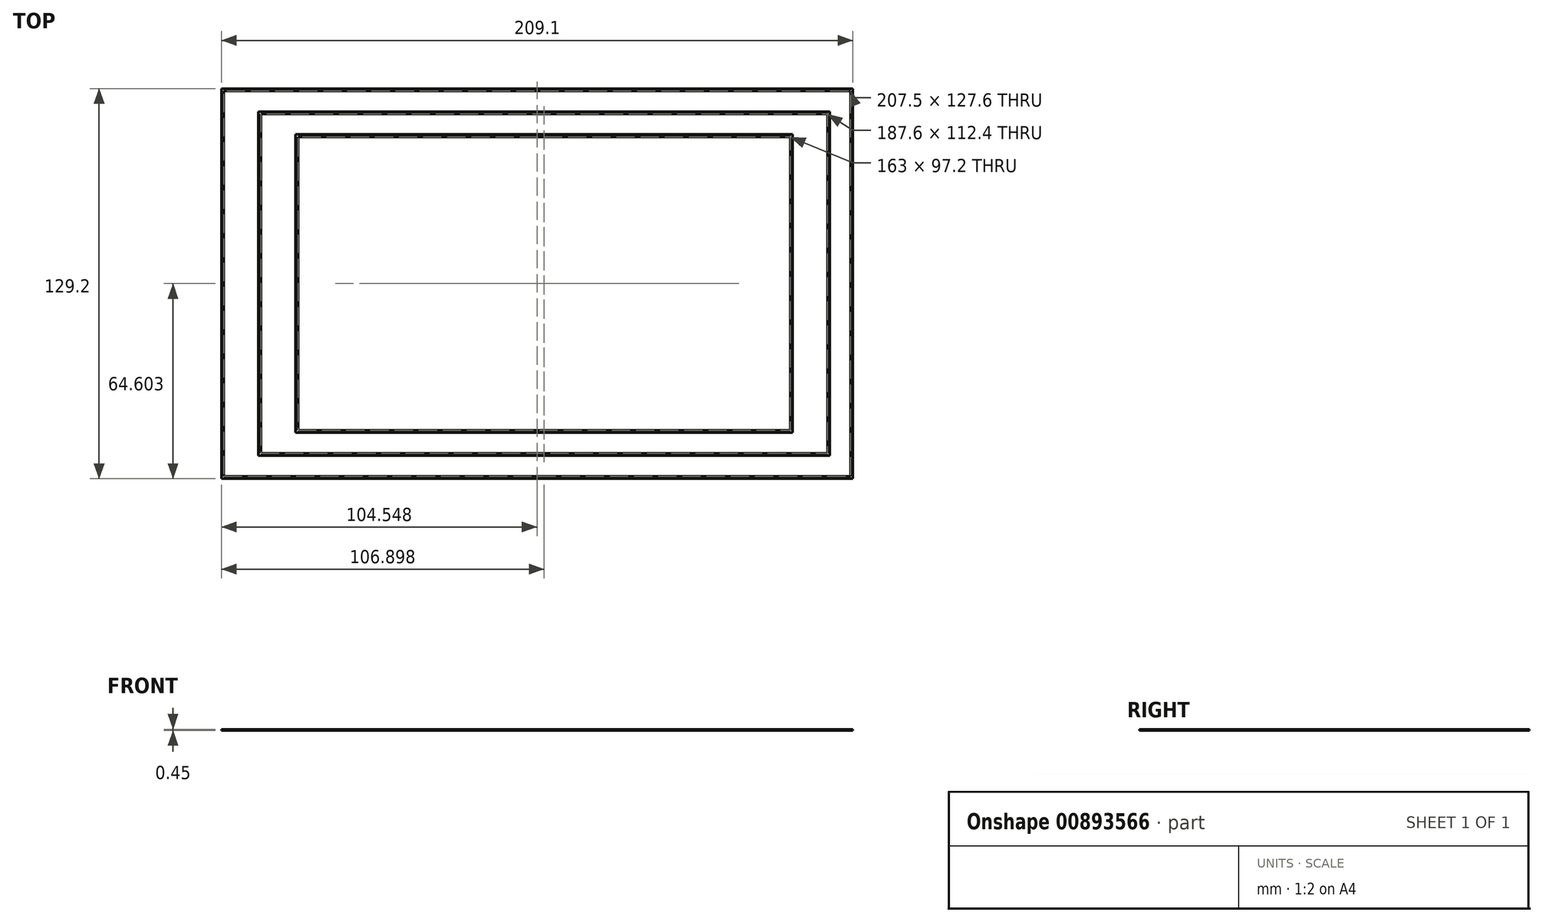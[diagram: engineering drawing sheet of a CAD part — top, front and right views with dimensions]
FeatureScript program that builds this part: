
annotation { "Feature Type Name" : "Feature", "Feature Type Description" : "" }
export const myFeature = defineFeature(function(context is Context, id is Id, definition is map)
    precondition{}
    {
        {
            assignVariable(context, id + "F0", {"name" : "LineHeight", "anyValue" : 0.15 * 3});
        }
        {
            var Q0;
            Q0=qCreatedBy(makeId("Top.planeOp"),FACE);
            var sketch = newSketch(context, id + "F1", { "sketchPlane" : qUnion([Q0])});
            skLineSegment(sketch, "E0.bottom", {"start": v(-91.48, 57.06) * mm, "end": v(117.62, 57.06) * mm});
            skLineSegment(sketch, "E0.top", {"start": v(-91.48, -72.14) * mm, "end": v(117.62, -72.14) * mm});
            skLineSegment(sketch, "E0.left", {"start": v(-91.48, 57.06) * mm, "end": v(-91.48, -72.14) * mm});
            skLineSegment(sketch, "E0.right", {"start": v(117.62, 57.06) * mm, "end": v(117.62, -72.14) * mm});
            skLineSegment(sketch, "E1.bottom", {"start": v(-79.18, 49.46) * mm, "end": v(110.02, 49.46) * mm});
            skLineSegment(sketch, "E1.top", {"start": v(-79.18, -64.54) * mm, "end": v(110.02, -64.54) * mm});
            skLineSegment(sketch, "E1.left", {"start": v(-79.18, 49.46) * mm, "end": v(-79.18, -64.54) * mm});
            skLineSegment(sketch, "E1.right", {"start": v(110.02, 49.46) * mm, "end": v(110.02, -64.54) * mm});
            skLineSegment(sketch, "E2.bottom", {"start": v(-66.88, 41.86) * mm, "end": v(97.72, 41.86) * mm});
            skLineSegment(sketch, "E2.top", {"start": v(-66.88, -56.94) * mm, "end": v(97.72, -56.94) * mm});
            skLineSegment(sketch, "E2.left", {"start": v(-66.88, 41.86) * mm, "end": v(-66.88, -56.94) * mm});
            skLineSegment(sketch, "E2.right", {"start": v(97.72, 41.86) * mm, "end": v(97.72, -56.94) * mm});
            skLineSegment(sketch, "E3", {"start": v(-90.68, 56.26) * mm, "end": v(116.82, 56.26) * mm});
            skLineSegment(sketch, "E4", {"start": v(116.82, 56.26) * mm, "end": v(116.82, -71.34) * mm});
            skLineSegment(sketch, "E5", {"start": v(116.82, -71.34) * mm, "end": v(-90.68, -71.34) * mm});
            skLineSegment(sketch, "E6", {"start": v(-90.68, -71.34) * mm, "end": v(-90.68, 56.26) * mm});
            skLineSegment(sketch, "E7", {"start": v(-78.38, 48.66) * mm, "end": v(109.22, 48.66) * mm});
            skLineSegment(sketch, "E8", {"start": v(109.22, 48.66) * mm, "end": v(109.22, -63.74) * mm});
            skLineSegment(sketch, "E9", {"start": v(109.22, -63.74) * mm, "end": v(-78.38, -63.74) * mm});
            skLineSegment(sketch, "E10", {"start": v(-78.38, -63.74) * mm, "end": v(-78.38, 48.66) * mm});
            skLineSegment(sketch, "E11", {"start": v(-66.08, 41.06) * mm, "end": v(96.92, 41.06) * mm});
            skLineSegment(sketch, "E12", {"start": v(96.92, 41.06) * mm, "end": v(96.92, -56.14) * mm});
            skLineSegment(sketch, "E13", {"start": v(96.92, -56.14) * mm, "end": v(-66.08, -56.14) * mm});
            skLineSegment(sketch, "E14", {"start": v(-66.08, -56.14) * mm, "end": v(-66.08, 41.06) * mm});
            skSolve(sketch);
        }
        {
            var Q0;
            {var subQ10=sQuery(id+"F1.wireOp",EDGE,"E1.top");Q0=makeQuery(id+"F1.imprint","IMPRINT",FACE,{"disambiguationData":[TD([[makeQuery(id+"F1.imprint","IMPRINT",EDGE,{"derivedFrom":subQ10}),1.0]])]});}
            var Q1;
            Q1=makeQuery(id+"F1.imprint","IMPRINT",FACE,{"disambiguationData":[TD([[makeQuery(id+"F1.imprint","IMPRINT",EDGE,{"derivedFrom":sQuery(id+"F1.wireOp",EDGE,"E0.bottom")}),-1.0]])]});
            var Q2;
            Q2=makeQuery(id+"F1.imprint","IMPRINT",FACE,{"disambiguationData":[TD([[makeQuery(id+"F1.imprint","IMPRINT",EDGE,{"derivedFrom":sQuery(id+"F1.wireOp",EDGE,"E2.bottom")}),-1.0]])]});
            var Q3;
            {var subQ0=sQuery(id+"F1.wireOp",EDGE,"HmofG7po-VB2C-NLRk-urQ5-j8slKDY0yj7J");Q3=makeQuery(id+"F1.imprint","IMPRINT",FACE,{"disambiguationData":[TD([[makeQuery(id+"F1.imprint","IMPRINT",EDGE,{"derivedFrom":subQ0}),1.0]])]});}
            var Q4;
            Q4=makeQuery(id+"F1.imprint","IMPRINT",FACE,{"disambiguationData":[TD([[makeQuery(id+"F1.imprint","IMPRINT",EDGE,{"derivedFrom":sQuery(id+"F1.wireOp",EDGE,"iO6pfZbY-7ntN-yKzr-tIri-R5R3f5lDf0fY")}),1.0]])]});
            extrude(context, id + "F2", {"entities" : qUnion([Q0, Q1, Q2, Q3, Q4]), "depth" : (getVariable(context, 'LineHeight')) * mm, "offsetDistance" : 25 * mm});
        }
    });
